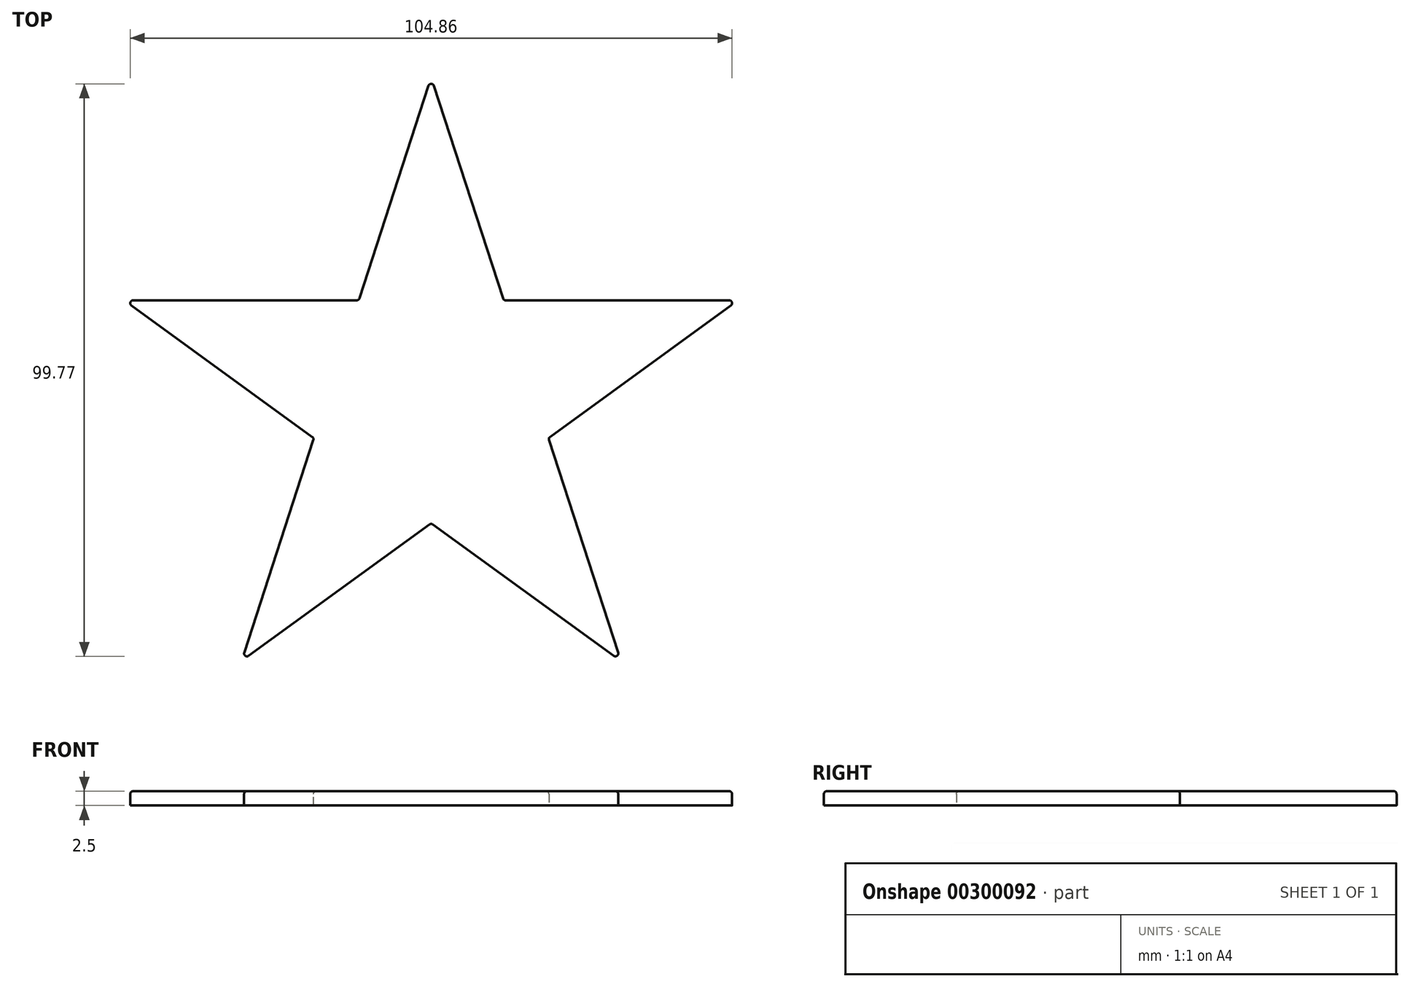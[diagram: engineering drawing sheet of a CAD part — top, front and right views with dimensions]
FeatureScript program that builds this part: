
annotation { "Feature Type Name" : "Feature", "Feature Type Description" : "" }
export const myFeature = defineFeature(function(context is Context, id is Id, definition is map)
    precondition{}
    {
        {
            var Q0;
            Q0=qCreatedBy(makeId("Top.planeOp"),FACE);
            var sketch = newSketch(context, id + "F0", { "sketchPlane" : qUnion([Q0])});
            skCircle(sketch, "E0.cCircle", {"center": v(0, 0) * mm, "radius": 56.22 * mm, "construction": true});
            skLineSegment(sketch, "E1", {"start": v(0, 56.22) * mm, "end": v(-33.04, -45.48) * mm});
            skLineSegment(sketch, "E2", {"start": v(-53.47, 17.37) * mm, "end": v(53.47, 17.37) * mm});
            skLineSegment(sketch, "E3", {"start": v(-53.47, 17.37) * mm, "end": v(33.04, -45.48) * mm});
            skLineSegment(sketch, "E4", {"start": v(33.04, -45.48) * mm, "end": v(0, 56.22) * mm});
            skLineSegment(sketch, "E5", {"start": v(53.47, 17.37) * mm, "end": v(-33.04, -45.48) * mm});
            skSolve(sketch);
        }
        {
            var Q0;
            {var subQ0=sQuery(id+"F0.wireOp",EDGE,"E2");var subQ1=sQuery(id+"F0.wireOp",EDGE,"E1");var subQ2=makeQuery(id+"F0.imprint","INTERSECT",VERTEX,{"derivedFrom":[subQ1,subQ0]});Q0=makeQuery(id+"F0.imprint","IMPRINT",FACE,{"disambiguationData":[TD([[makeQuery(id+"F0.imprint","IMPRINT",EDGE,{"disambiguationData":[TD([[subQ2,-1.0]])],"derivedFrom":subQ1}),-1.0]])]});}
            var Q1;
            {var subQ0=sQuery(id+"F0.wireOp",EDGE,"E4");var subQ1=sQuery(id+"F0.wireOp",EDGE,"E1");var subQ2=makeQuery(id+"F0.imprint","INTERSECT",VERTEX,{"derivedFrom":[subQ1,subQ0]});Q1=makeQuery(id+"F0.imprint","IMPRINT",FACE,{"disambiguationData":[TD([[makeQuery(id+"F0.imprint","IMPRINT",EDGE,{"disambiguationData":[TD([[subQ2,-1.0]])],"derivedFrom":subQ1}),1.0]])]});}
            var Q2;
            {var subQ1=sQuery(id+"F0.wireOp",EDGE,"E2");var subQ6=sQuery(id+"F0.wireOp",EDGE,"E1");var subQ9=makeQuery(id+"F0.imprint","INTERSECT",VERTEX,{"derivedFrom":[subQ6,subQ1]});Q2=makeQuery(id+"F0.imprint","IMPRINT",FACE,{"disambiguationData":[TD([[makeQuery(id+"F0.imprint","IMPRINT",EDGE,{"disambiguationData":[TD([[subQ9,-1.0]])],"derivedFrom":subQ6}),1.0]])]});}
            var Q3;
            {var subQ0=sQuery(id+"F0.wireOp",EDGE,"E5");var subQ1=sQuery(id+"F0.wireOp",EDGE,"E2");var subQ2=makeQuery(id+"F0.imprint","INTERSECT",VERTEX,{"derivedFrom":[subQ1,subQ0]});Q3=makeQuery(id+"F0.imprint","IMPRINT",FACE,{"disambiguationData":[TD([[makeQuery(id+"F0.imprint","IMPRINT",EDGE,{"disambiguationData":[TD([[subQ2,1.0]])],"derivedFrom":subQ1}),-1.0]])]});}
            var Q4;
            {var subQ0=sQuery(id+"F0.wireOp",EDGE,"E4");var subQ1=sQuery(id+"F0.wireOp",EDGE,"E3");var subQ2=makeQuery(id+"F0.imprint","INTERSECT",VERTEX,{"derivedFrom":[subQ1,subQ0]});Q4=makeQuery(id+"F0.imprint","IMPRINT",FACE,{"disambiguationData":[TD([[makeQuery(id+"F0.imprint","IMPRINT",EDGE,{"disambiguationData":[TD([[subQ2,1.0]])],"derivedFrom":subQ1}),1.0]])]});}
            var Q5;
            {var subQ0=sQuery(id+"F0.wireOp",EDGE,"E5");var subQ1=sQuery(id+"F0.wireOp",EDGE,"E1");var subQ2=makeQuery(id+"F0.imprint","INTERSECT",VERTEX,{"derivedFrom":[subQ1,subQ0]});Q5=makeQuery(id+"F0.imprint","IMPRINT",FACE,{"disambiguationData":[TD([[makeQuery(id+"F0.imprint","IMPRINT",EDGE,{"disambiguationData":[TD([[subQ2,1.0]])],"derivedFrom":subQ1}),1.0]])]});}
            extrude(context, id + "F1", {"entities" : qUnion([Q0, Q1, Q2, Q3, Q4, Q5]), "depth" : 2.5 * mm});
        }
        {
            var Q0;
            Q0=makeQuery(id+"F1.opExtrude","SWEPT_EDGE",EDGE,{"disambiguationData":[OSD([sQuery(id+"F0.wireOp",EDGE,"E1"),sQuery(id+"F0.wireOp",EDGE,"E4")])]});
            var Q1;
            Q1=makeQuery(id+"F1.opExtrude","SWEPT_EDGE",EDGE,{"disambiguationData":[OSD([sQuery(id+"F0.wireOp",EDGE,"E2"),sQuery(id+"F0.wireOp",EDGE,"E3")])]});
            var Q2;
            Q2=makeQuery(id+"F1.opExtrude","SWEPT_EDGE",EDGE,{"disambiguationData":[OSD([sQuery(id+"F0.wireOp",EDGE,"E1"),sQuery(id+"F0.wireOp",EDGE,"E5")])]});
            var Q3;
            Q3=makeQuery(id+"F1.opExtrude","SWEPT_EDGE",EDGE,{"disambiguationData":[OSD([sQuery(id+"F0.wireOp",EDGE,"E3"),sQuery(id+"F0.wireOp",EDGE,"E4")])]});
            var Q4;
            Q4=makeQuery(id+"F1.opExtrude","SWEPT_EDGE",EDGE,{"disambiguationData":[OSD([sQuery(id+"F0.wireOp",EDGE,"E2"),sQuery(id+"F0.wireOp",EDGE,"E5")])]});
            var Q5;
            Q5=makeQuery(id+"F1.opExtrude","SWEPT_EDGE",EDGE,{"disambiguationData":[OSD([sQuery(id+"F0.wireOp",EDGE,"E1"),sQuery(id+"F0.wireOp",EDGE,"E3")])]});
            var Q6;
            Q6=makeQuery(id+"F1.opExtrude","SWEPT_EDGE",EDGE,{"disambiguationData":[OSD([sQuery(id+"F0.wireOp",EDGE,"E1"),sQuery(id+"F0.wireOp",EDGE,"E2")])]});
            var Q7;
            Q7=makeQuery(id+"F1.opExtrude","SWEPT_EDGE",EDGE,{"disambiguationData":[OSD([sQuery(id+"F0.wireOp",EDGE,"E2"),sQuery(id+"F0.wireOp",EDGE,"E4")])]});
            var Q8;
            Q8=makeQuery(id+"F1.opExtrude","SWEPT_EDGE",EDGE,{"disambiguationData":[OSD([sQuery(id+"F0.wireOp",EDGE,"E4"),sQuery(id+"F0.wireOp",EDGE,"E5")])]});
            var Q9;
            Q9=makeQuery(id+"F1.opExtrude","SWEPT_EDGE",EDGE,{"disambiguationData":[OSD([sQuery(id+"F0.wireOp",EDGE,"E3"),sQuery(id+"F0.wireOp",EDGE,"E5")])]});
            fillet(context, id + "F2", {"entities" : qUnion([Q0, Q1, Q2, Q3, Q4, Q5, Q6, Q7, Q8, Q9]), "radius" : 0.5 * mm, "tangentPropagation" : true, "allowEdgeOverflow" : false});
        }
        {
            var Q0;
            {var subQ0=sQuery(id+"F0.wireOp",EDGE,"E4");Q0=makeQuery(id+"F1.opExtrude","CAP_EDGE",EDGE,{"disambiguationData":[OSD([subQ0]),TDD([makeQuery(id+"F0.imprint","IMPRINT",EDGE,{"disambiguationData":[TD([[makeQuery(id+"F0.imprint","INTERSECT",VERTEX,{"derivedFrom":[sQuery(id+"F0.wireOp",EDGE,"E1"),subQ0]}),1.0]])],"derivedFrom":subQ0})])],"isStart":false});}
            var Q1;
            {var subQ0=sQuery(id+"F0.wireOp",EDGE,"E1");Q1=makeQuery(id+"F1.opExtrude","CAP_EDGE",EDGE,{"disambiguationData":[OSD([subQ0]),TDD([makeQuery(id+"F0.imprint","IMPRINT",EDGE,{"disambiguationData":[TD([[makeQuery(id+"F0.imprint","INTERSECT",VERTEX,{"derivedFrom":[subQ0,sQuery(id+"F0.wireOp",EDGE,"E4")]}),-1.0]])],"derivedFrom":subQ0})])],"isStart":false});}
            var Q2;
            {var subQ0=sQuery(id+"F0.wireOp",EDGE,"E2");Q2=makeQuery(id+"F1.opExtrude","CAP_EDGE",EDGE,{"disambiguationData":[OSD([subQ0]),TDD([makeQuery(id+"F0.imprint","IMPRINT",EDGE,{"disambiguationData":[TD([[makeQuery(id+"F0.imprint","INTERSECT",VERTEX,{"derivedFrom":[subQ0,sQuery(id+"F0.wireOp",EDGE,"E5")]}),1.0]])],"derivedFrom":subQ0})])],"isStart":false});}
            var Q3;
            {var subQ0=sQuery(id+"F0.wireOp",EDGE,"E5");Q3=makeQuery(id+"F1.opExtrude","CAP_EDGE",EDGE,{"disambiguationData":[OSD([subQ0]),TDD([makeQuery(id+"F0.imprint","IMPRINT",EDGE,{"disambiguationData":[TD([[makeQuery(id+"F0.imprint","INTERSECT",VERTEX,{"derivedFrom":[sQuery(id+"F0.wireOp",EDGE,"E2"),subQ0]}),-1.0]])],"derivedFrom":subQ0})])],"isStart":false});}
            var Q4;
            {var subQ0=sQuery(id+"F0.wireOp",EDGE,"E4");Q4=makeQuery(id+"F1.opExtrude","CAP_EDGE",EDGE,{"disambiguationData":[OSD([subQ0]),TDD([makeQuery(id+"F0.imprint","IMPRINT",EDGE,{"disambiguationData":[TD([[makeQuery(id+"F0.imprint","INTERSECT",VERTEX,{"derivedFrom":[sQuery(id+"F0.wireOp",EDGE,"E3"),subQ0]}),-1.0]])],"derivedFrom":subQ0})])],"isStart":false});}
            var Q5;
            {var subQ0=sQuery(id+"F0.wireOp",EDGE,"E3");Q5=makeQuery(id+"F1.opExtrude","CAP_EDGE",EDGE,{"disambiguationData":[OSD([subQ0]),TDD([makeQuery(id+"F0.imprint","IMPRINT",EDGE,{"disambiguationData":[TD([[makeQuery(id+"F0.imprint","INTERSECT",VERTEX,{"derivedFrom":[subQ0,sQuery(id+"F0.wireOp",EDGE,"E4")]}),1.0]])],"derivedFrom":subQ0})])],"isStart":false});}
            var Q6;
            {var subQ0=sQuery(id+"F0.wireOp",EDGE,"E5");Q6=makeQuery(id+"F1.opExtrude","CAP_EDGE",EDGE,{"disambiguationData":[OSD([subQ0]),TDD([makeQuery(id+"F0.imprint","IMPRINT",EDGE,{"disambiguationData":[TD([[makeQuery(id+"F0.imprint","INTERSECT",VERTEX,{"derivedFrom":[sQuery(id+"F0.wireOp",EDGE,"E1"),subQ0]}),1.0]])],"derivedFrom":subQ0})])],"isStart":false});}
            var Q7;
            {var subQ0=sQuery(id+"F0.wireOp",EDGE,"E1");Q7=makeQuery(id+"F1.opExtrude","CAP_EDGE",EDGE,{"disambiguationData":[OSD([subQ0]),TDD([makeQuery(id+"F0.imprint","IMPRINT",EDGE,{"disambiguationData":[TD([[makeQuery(id+"F0.imprint","INTERSECT",VERTEX,{"derivedFrom":[subQ0,sQuery(id+"F0.wireOp",EDGE,"E5")]}),1.0]])],"derivedFrom":subQ0})])],"isStart":false});}
            var Q8;
            {var subQ0=sQuery(id+"F0.wireOp",EDGE,"E3");Q8=makeQuery(id+"F1.opExtrude","CAP_EDGE",EDGE,{"disambiguationData":[OSD([subQ0]),TDD([makeQuery(id+"F0.imprint","IMPRINT",EDGE,{"disambiguationData":[TD([[makeQuery(id+"F0.imprint","INTERSECT",VERTEX,{"derivedFrom":[sQuery(id+"F0.wireOp",EDGE,"E2"),subQ0]}),-1.0]])],"derivedFrom":subQ0})])],"isStart":false});}
            var Q9;
            {var subQ0=sQuery(id+"F0.wireOp",EDGE,"E2");Q9=makeQuery(id+"F1.opExtrude","CAP_EDGE",EDGE,{"disambiguationData":[OSD([subQ0]),TDD([makeQuery(id+"F0.imprint","IMPRINT",EDGE,{"disambiguationData":[TD([[makeQuery(id+"F0.imprint","INTERSECT",VERTEX,{"derivedFrom":[subQ0,sQuery(id+"F0.wireOp",EDGE,"E3")]}),-1.0]])],"derivedFrom":subQ0})])],"isStart":false});}
            var Q10;
            {var subQ0=sQuery(id+"F0.wireOp",EDGE,"E5");var subQ1=sQuery(id+"F0.wireOp",EDGE,"E1");Q10=makeQuery(id+"F2.opFillet","BLEND_EDGE",EDGE,{"blendedFrom":[makeQuery(id+"F1.opExtrude","SWEPT_EDGE",EDGE,{"disambiguationData":[OSD([subQ1,subQ0])]}),makeQuery(id+"F1.opExtrude","CAP_FACE",FACE,{"disambiguationData":[OSD([subQ1,sQuery(id+"F0.wireOp",EDGE,"E2"),sQuery(id+"F0.wireOp",EDGE,"E3"),sQuery(id+"F0.wireOp",EDGE,"E4"),subQ0])],"isStart":false})],"blendedInto":[makeQuery(id+"F1.opExtrude","CAP_FACE",FACE,{"disambiguationData":[OSD([subQ1,sQuery(id+"F0.wireOp",EDGE,"E2"),sQuery(id+"F0.wireOp",EDGE,"E3"),sQuery(id+"F0.wireOp",EDGE,"E4"),subQ0])],"isStart":false})]});}
            var Q11;
            {var subQ0=sQuery(id+"F0.wireOp",EDGE,"E4");var subQ1=sQuery(id+"F0.wireOp",EDGE,"E3");Q11=makeQuery(id+"F2.opFillet","BLEND_EDGE",EDGE,{"blendedFrom":[makeQuery(id+"F1.opExtrude","SWEPT_EDGE",EDGE,{"disambiguationData":[OSD([subQ1,subQ0])]}),makeQuery(id+"F1.opExtrude","CAP_FACE",FACE,{"disambiguationData":[OSD([sQuery(id+"F0.wireOp",EDGE,"E1"),sQuery(id+"F0.wireOp",EDGE,"E2"),subQ1,subQ0,sQuery(id+"F0.wireOp",EDGE,"E5")])],"isStart":false})],"blendedInto":[makeQuery(id+"F1.opExtrude","CAP_FACE",FACE,{"disambiguationData":[OSD([sQuery(id+"F0.wireOp",EDGE,"E1"),sQuery(id+"F0.wireOp",EDGE,"E2"),subQ1,subQ0,sQuery(id+"F0.wireOp",EDGE,"E5")])],"isStart":false})]});}
            var Q12;
            {var subQ0=sQuery(id+"F0.wireOp",EDGE,"E5");var subQ1=sQuery(id+"F0.wireOp",EDGE,"E2");Q12=makeQuery(id+"F2.opFillet","BLEND_EDGE",EDGE,{"blendedFrom":[makeQuery(id+"F1.opExtrude","SWEPT_EDGE",EDGE,{"disambiguationData":[OSD([subQ1,subQ0])]}),makeQuery(id+"F1.opExtrude","CAP_FACE",FACE,{"disambiguationData":[OSD([sQuery(id+"F0.wireOp",EDGE,"E1"),subQ1,sQuery(id+"F0.wireOp",EDGE,"E3"),sQuery(id+"F0.wireOp",EDGE,"E4"),subQ0])],"isStart":false})],"blendedInto":[makeQuery(id+"F1.opExtrude","CAP_FACE",FACE,{"disambiguationData":[OSD([sQuery(id+"F0.wireOp",EDGE,"E1"),subQ1,sQuery(id+"F0.wireOp",EDGE,"E3"),sQuery(id+"F0.wireOp",EDGE,"E4"),subQ0])],"isStart":false})]});}
            var Q13;
            {var subQ0=sQuery(id+"F0.wireOp",EDGE,"E4");var subQ1=sQuery(id+"F0.wireOp",EDGE,"E1");Q13=makeQuery(id+"F2.opFillet","BLEND_EDGE",EDGE,{"blendedFrom":[makeQuery(id+"F1.opExtrude","SWEPT_EDGE",EDGE,{"disambiguationData":[OSD([subQ1,subQ0])]}),makeQuery(id+"F1.opExtrude","CAP_FACE",FACE,{"disambiguationData":[OSD([subQ1,sQuery(id+"F0.wireOp",EDGE,"E2"),sQuery(id+"F0.wireOp",EDGE,"E3"),subQ0,sQuery(id+"F0.wireOp",EDGE,"E5")])],"isStart":false})],"blendedInto":[makeQuery(id+"F1.opExtrude","CAP_FACE",FACE,{"disambiguationData":[OSD([subQ1,sQuery(id+"F0.wireOp",EDGE,"E2"),sQuery(id+"F0.wireOp",EDGE,"E3"),subQ0,sQuery(id+"F0.wireOp",EDGE,"E5")])],"isStart":false})]});}
            var Q14;
            {var subQ0=sQuery(id+"F0.wireOp",EDGE,"E3");var subQ1=sQuery(id+"F0.wireOp",EDGE,"E2");Q14=makeQuery(id+"F2.opFillet","BLEND_EDGE",EDGE,{"blendedFrom":[makeQuery(id+"F1.opExtrude","SWEPT_EDGE",EDGE,{"disambiguationData":[OSD([subQ1,subQ0])]}),makeQuery(id+"F1.opExtrude","CAP_FACE",FACE,{"disambiguationData":[OSD([sQuery(id+"F0.wireOp",EDGE,"E1"),subQ1,subQ0,sQuery(id+"F0.wireOp",EDGE,"E4"),sQuery(id+"F0.wireOp",EDGE,"E5")])],"isStart":false})],"blendedInto":[makeQuery(id+"F1.opExtrude","CAP_FACE",FACE,{"disambiguationData":[OSD([sQuery(id+"F0.wireOp",EDGE,"E1"),subQ1,subQ0,sQuery(id+"F0.wireOp",EDGE,"E4"),sQuery(id+"F0.wireOp",EDGE,"E5")])],"isStart":false})]});}
            fillet(context, id + "F3", {"entities" : qUnion([Q0, Q1, Q2, Q3, Q4, Q5, Q6, Q7, Q8, Q9, Q10, Q11, Q12, Q13, Q14]), "radius" : 0.5 * mm, "tangentPropagation" : true, "allowEdgeOverflow" : false});
        }
    });
